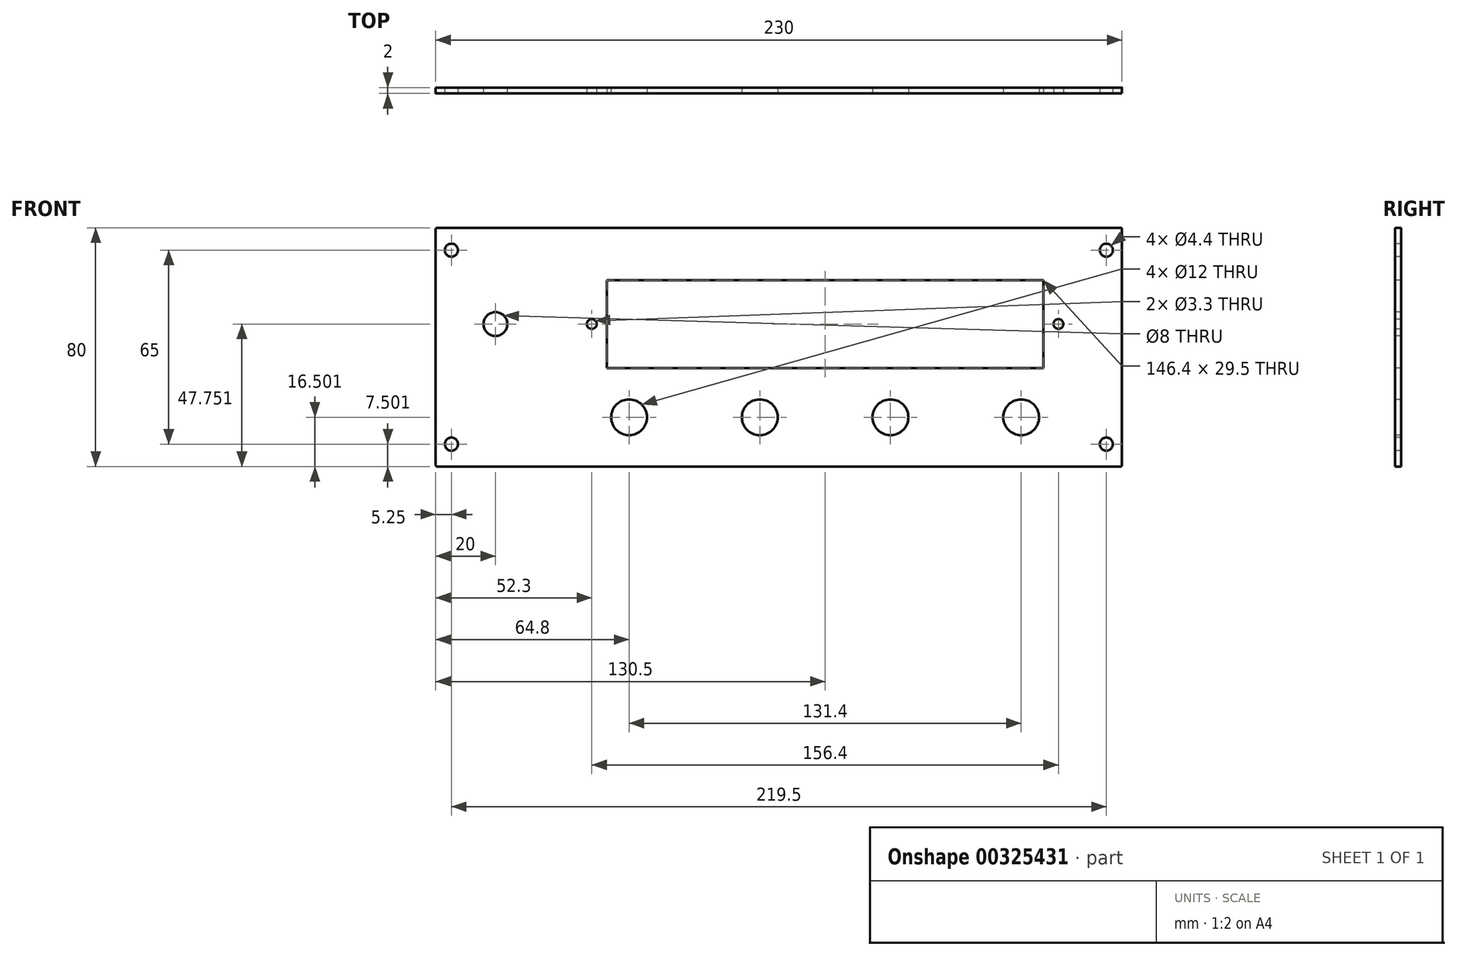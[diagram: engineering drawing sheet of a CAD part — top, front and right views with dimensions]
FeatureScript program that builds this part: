
annotation { "Feature Type Name" : "Feature", "Feature Type Description" : "" }
export const myFeature = defineFeature(function(context is Context, id is Id, definition is map)
    precondition{}
    {
        {
            var Q0;
            Q0=qCreatedBy(makeId("Front.planeOp"),FACE);
            var sketch = newSketch(context, id + "F0", { "sketchPlane" : qUnion([Q0])});
            skLineSegment(sketch, "E0.bottom", {"start": v(-114.5, 12.9) * mm, "end": v(114.5, 12.9) * mm});
            skLineSegment(sketch, "E0.top", {"start": v(-114.5, -67.1) * mm, "end": v(114.5, -67.1) * mm});
            skLineSegment(sketch, "E0.left", {"start": v(-115, 12.4) * mm, "end": v(-115, -66.6) * mm});
            skLineSegment(sketch, "E0.right", {"start": v(115, 12.4) * mm, "end": v(115, -66.6) * mm});
            skLineSegment(sketch, "E1", {"start": v(-115, 5.4) * mm, "end": v(115, 5.4) * mm, "construction": true});
            skLineSegment(sketch, "E2", {"start": v(-109.75, 12.9) * mm, "end": v(-109.75, -67.1) * mm, "construction": true});
            skPoint(sketch, "E3", {"position": v(-109.75, 5.4) * mm});
            skLineSegment(sketch, "E4.bottom", {"start": v(-57.7, -4.6) * mm, "end": v(88.7, -4.6) * mm});
            skLineSegment(sketch, "E4.top", {"start": v(-57.7, -34.1) * mm, "end": v(88.7, -34.1) * mm});
            skLineSegment(sketch, "E4.left", {"start": v(-57.7, -4.6) * mm, "end": v(-57.7, -34.1) * mm});
            skLineSegment(sketch, "E4.right", {"start": v(88.7, -4.6) * mm, "end": v(88.7, -34.1) * mm});
            skLineSegment(sketch, "E5", {"start": v(-62.7, -4.6) * mm, "end": v(-62.7, -34.1) * mm, "construction": true});
            skLineSegment(sketch, "E6", {"start": v(15.5, -4.6) * mm, "end": v(15.5, -34.1) * mm, "construction": true});
            skPoint(sketch, "E7", {"position": v(-62.7, -19.36) * mm});
            skPoint(sketch, "E8.MirrorP", {"position": v(93.7, -19.36) * mm});
            skLineSegment(sketch, "E9", {"start": v(0, 12.9) * mm, "end": v(0, -67.1) * mm, "construction": true});
            skLineSegment(sketch, "E10", {"start": v(-105, 12.9) * mm, "end": v(-105, -67.1) * mm, "construction": true});
            skLineSegment(sketch, "E11.MirrorCS", {"start": v(105, 12.9) * mm, "end": v(105, -67.1) * mm, "construction": true});
            skLineSegment(sketch, "E12.bottom", {"start": v(-66, -3.6) * mm, "end": v(97, -3.6) * mm, "construction": true});
            skLineSegment(sketch, "E12.top", {"start": v(-66, -35.1) * mm, "end": v(97, -35.1) * mm, "construction": true});
            skLineSegment(sketch, "E12.left", {"start": v(-66, -3.6) * mm, "end": v(-66, -35.1) * mm, "construction": true});
            skLineSegment(sketch, "E12.right", {"start": v(97, -3.6) * mm, "end": v(97, -35.1) * mm, "construction": true});
            skPoint(sketch, "E13", {"position": v(15.5, -3.6) * mm});
            skPoint(sketch, "E14", {"position": v(97, -19.36) * mm});
            skLineSegment(sketch, "E15", {"start": v(-62.7, -19.36) * mm, "end": v(93.7, -19.36) * mm, "construction": true});
            skPoint(sketch, "E16", {"position": v(-109.75, -59.6) * mm});
            skPoint(sketch, "E17.MirrorP", {"position": v(109.75, 5.4) * mm});
            skPoint(sketch, "E18.MirrorP", {"position": v(109.75, -59.6) * mm});
            skLineSegment(sketch, "E19", {"start": v(-105, -50.6) * mm, "end": v(105, -50.6) * mm, "construction": true});
            skPoint(sketch, "E20", {"position": v(-95, -19.36) * mm});
            skCircle(sketch, "E21", {"center": v(-95, -19.36) * mm, "radius": 6 * mm, "construction": true});
            skCircle(sketch, "E22", {"center": v(81.2, -50.6) * mm, "radius": 7.5 * mm, "construction": true});
            skCircle(sketch, "E23.1.0.0", {"center": v(37.4, -50.6) * mm, "radius": 7.5 * mm, "construction": true});
            skCircle(sketch, "E23.2.0.0", {"center": v(-6.4, -50.6) * mm, "radius": 7.5 * mm, "construction": true});
            skCircle(sketch, "E23.3.0.0", {"center": v(-50.2, -50.6) * mm, "radius": 7.5 * mm, "construction": true});
            skLineSegment(sketch, "E23.direction1", {"start": v(81.2, -50.6) * mm, "end": v(37.4, -50.6) * mm, "construction": true});
            skPoint(sketch, "E24.visualSharp", {"position": v(-115, 12.9) * mm});
            skArc(sketch, "E24.filletArc", {"start": v(-114.5, 12.9) * mm, "mid": v(-114.85, 12.74) * mm, "end": v(-115, 12.4) * mm});
            skPoint(sketch, "E25.visualSharp", {"position": v(-115, -67.1) * mm});
            skArc(sketch, "E25.filletArc", {"start": v(-115, -66.6) * mm, "mid": v(-114.85, -66.96) * mm, "end": v(-114.5, -67.1) * mm});
            skPoint(sketch, "E26.visualSharp", {"position": v(115, -67.1) * mm});
            skArc(sketch, "E26.filletArc", {"start": v(114.5, -67.1) * mm, "mid": v(114.85, -66.96) * mm, "end": v(115, -66.6) * mm});
            skPoint(sketch, "E27.visualSharp", {"position": v(115, 12.9) * mm});
            skArc(sketch, "E27.filletArc", {"start": v(115, 12.4) * mm, "mid": v(114.85, 12.74) * mm, "end": v(114.5, 12.9) * mm});
            skSolve(sketch);
        }
        {
            var Q0;
            Q0=makeQuery(id+"F0.imprint","IMPRINT",FACE,{"disambiguationData":[TD([[makeQuery(id+"F0.imprint","IMPRINT",EDGE,{"derivedFrom":sQuery(id+"F0.wireOp",EDGE,"E0.bottom")}),-1.0]])]});
            extrude(context, id + "F1", {"entities" : qUnion([Q0]), "oppositeDirection" : true, "depth" : 2 * mm});
        }
        {
            var Q0;
            Q0=sQuery(id+"F0.wireOp",VERTEX,"E3");
            var Q1;
            Q1=sQuery(id+"F0.wireOp",VERTEX,"E17.MirrorP");
            var Q2;
            Q2=sQuery(id+"F0.wireOp",VERTEX,"E18.MirrorP");
            var Q3;
            Q3=sQuery(id+"F0.wireOp",VERTEX,"E16");
            var Q4;
            Q4=makeQuery(id+"F1.opExtrude","SWEPT_BODY",BODY,{"disambiguationData":[OSD([sQuery(id+"F0.wireOp",EDGE,"E0.bottom"),sQuery(id+"F0.wireOp",EDGE,"E0.top"),sQuery(id+"F0.wireOp",EDGE,"E0.left"),sQuery(id+"F0.wireOp",EDGE,"E0.right"),sQuery(id+"F0.wireOp",EDGE,"wUSLe2jA-Vntq-9wAi-NqRe-D4dN2Iv6WiXZ"),sQuery(id+"F0.wireOp",EDGE,"0V3KryEC-EEOE-b1Vl-SPv9-SGiPuqfbHOCA"),sQuery(id+"F0.wireOp",EDGE,"VXoqg1l5-3Q0s-zM9H-MVhQ-kMZ0NWrAAzfJ")])]});
            hole(context, id + "F2", {"style" : HoleStyle.SIMPLE, "endStyle" : HoleEndStyle.THROUGH, "standardTappedOrClearance" : lookupTablePath({ "standard" : "ISO", "fit" : "Normal", "size" : "M4", "type" : "Clearance" }), "standardBlindInLast" : lookupTablePath({ "fit" : "Standard", "standard" : "ISO", "size" : "M4", "type" : "Clearance" }), "holeDiameter" : 4.4 * mm, "tappedDepth" : 12 * mm, "tapClearance" : 3, "locations" : qUnion([Q0, Q1, Q2, Q3]), "scope" : qUnion([Q4])});
        }
        {
            var Q0;
            Q0=sQuery(id+"F0.wireOp",VERTEX,"E7");
            var Q1;
            Q1=sQuery(id+"F0.wireOp",VERTEX,"E8.MirrorP");
            var Q2;
            Q2=makeQuery(id+"F1.opExtrude","SWEPT_BODY",BODY,{"disambiguationData":[OSD([sQuery(id+"F0.wireOp",EDGE,"E0.bottom"),sQuery(id+"F0.wireOp",EDGE,"E0.top"),sQuery(id+"F0.wireOp",EDGE,"E0.left"),sQuery(id+"F0.wireOp",EDGE,"E0.right"),sQuery(id+"F0.wireOp",EDGE,"E4.bottom"),sQuery(id+"F0.wireOp",EDGE,"E4.top"),sQuery(id+"F0.wireOp",EDGE,"E4.left"),sQuery(id+"F0.wireOp",EDGE,"E4.right")])]});
            hole(context, id + "F3", {"style" : HoleStyle.SIMPLE, "endStyle" : HoleEndStyle.THROUGH, "standardTappedOrClearance" : lookupTablePath({ "standard" : "ISO", "fit" : "Normal", "size" : "M3", "type" : "Clearance" }), "standardBlindInLast" : lookupTablePath({ "fit" : "Standard", "standard" : "ISO", "size" : "M3", "type" : "Clearance" }), "holeDiameter" : 3.3 * mm, "tappedDepth" : 12 * mm, "tapClearance" : 3, "locations" : qUnion([Q0, Q1]), "scope" : qUnion([Q2])});
        }
        {
            var Q0;
            Q0=sQuery(id+"F0.wireOp",VERTEX,"E20");
            var Q1;
            Q1=makeQuery(id+"F1.opExtrude","SWEPT_BODY",BODY,{"disambiguationData":[OSD([sQuery(id+"F0.wireOp",EDGE,"E0.bottom"),sQuery(id+"F0.wireOp",EDGE,"E0.top"),sQuery(id+"F0.wireOp",EDGE,"E0.left"),sQuery(id+"F0.wireOp",EDGE,"E0.right"),sQuery(id+"F0.wireOp",EDGE,"E4.bottom"),sQuery(id+"F0.wireOp",EDGE,"E4.top"),sQuery(id+"F0.wireOp",EDGE,"E4.left"),sQuery(id+"F0.wireOp",EDGE,"E4.right")])]});
            hole(context, id + "F4", {"style" : HoleStyle.SIMPLE, "endStyle" : HoleEndStyle.THROUGH, "holeDiameter" : 8 * mm, "tappedDepth" : 12 * mm, "tapClearance" : 3, "locations" : qUnion([Q0]), "scope" : qUnion([Q1])});
        }
        {
            var Q0;
            Q0=sQuery(id+"F0.wireOp",VERTEX,"E23.3.0.0.center");
            var Q1;
            Q1=sQuery(id+"F0.wireOp",VERTEX,"E23.2.0.0.center");
            var Q2;
            Q2=sQuery(id+"F0.wireOp",VERTEX,"E23.direction1.end");
            var Q3;
            Q3=sQuery(id+"F0.wireOp",VERTEX,"E22.center");
            var Q4;
            Q4=makeQuery(id+"F1.opExtrude","SWEPT_BODY",BODY,{"disambiguationData":[OSD([sQuery(id+"F0.wireOp",EDGE,"E0.bottom"),sQuery(id+"F0.wireOp",EDGE,"E0.top"),sQuery(id+"F0.wireOp",EDGE,"E0.left"),sQuery(id+"F0.wireOp",EDGE,"E0.right"),sQuery(id+"F0.wireOp",EDGE,"E4.bottom"),sQuery(id+"F0.wireOp",EDGE,"E4.top"),sQuery(id+"F0.wireOp",EDGE,"E4.left"),sQuery(id+"F0.wireOp",EDGE,"E4.right"),sQuery(id+"F0.wireOp",EDGE,"be85724a-6f3b-4295-9a29-0f0e669f6d4a.sketch_text.stroke-0"),sQuery(id+"F0.wireOp",EDGE,"be85724a-6f3b-4295-9a29-0f0e669f6d4a.sketch_text.stroke-1"),sQuery(id+"F0.wireOp",EDGE,"be85724a-6f3b-4295-9a29-0f0e669f6d4a.sketch_text.stroke-2"),sQuery(id+"F0.wireOp",EDGE,"be85724a-6f3b-4295-9a29-0f0e669f6d4a.sketch_text.stroke-3"),sQuery(id+"F0.wireOp",EDGE,"be85724a-6f3b-4295-9a29-0f0e669f6d4a.sketch_text.stroke-4"),sQuery(id+"F0.wireOp",EDGE,"be85724a-6f3b-4295-9a29-0f0e669f6d4a.sketch_text.stroke-5"),sQuery(id+"F0.wireOp",EDGE,"be85724a-6f3b-4295-9a29-0f0e669f6d4a.sketch_text.stroke-6"),sQuery(id+"F0.wireOp",EDGE,"be85724a-6f3b-4295-9a29-0f0e669f6d4a.sketch_text.stroke-7"),sQuery(id+"F0.wireOp",EDGE,"be85724a-6f3b-4295-9a29-0f0e669f6d4a.sketch_text.stroke-8"),sQuery(id+"F0.wireOp",EDGE,"be85724a-6f3b-4295-9a29-0f0e669f6d4a.sketch_text.stroke-9"),sQuery(id+"F0.wireOp",EDGE,"be85724a-6f3b-4295-9a29-0f0e669f6d4a.sketch_text.stroke-10"),sQuery(id+"F0.wireOp",EDGE,"be85724a-6f3b-4295-9a29-0f0e669f6d4a.sketch_text.stroke-11"),sQuery(id+"F0.wireOp",EDGE,"be85724a-6f3b-4295-9a29-0f0e669f6d4a.sketch_text.stroke-12"),sQuery(id+"F0.wireOp",EDGE,"be85724a-6f3b-4295-9a29-0f0e669f6d4a.sketch_text.stroke-13"),sQuery(id+"F0.wireOp",EDGE,"be85724a-6f3b-4295-9a29-0f0e669f6d4a.sketch_text.stroke-14"),sQuery(id+"F0.wireOp",EDGE,"be85724a-6f3b-4295-9a29-0f0e669f6d4a.sketch_text.stroke-15"),sQuery(id+"F0.wireOp",EDGE,"be85724a-6f3b-4295-9a29-0f0e669f6d4a.sketch_text.stroke-16"),sQuery(id+"F0.wireOp",EDGE,"be85724a-6f3b-4295-9a29-0f0e669f6d4a.sketch_text.stroke-17"),sQuery(id+"F0.wireOp",EDGE,"be85724a-6f3b-4295-9a29-0f0e669f6d4a.sketch_text.stroke-18"),sQuery(id+"F0.wireOp",EDGE,"be85724a-6f3b-4295-9a29-0f0e669f6d4a.sketch_text.stroke-19"),sQuery(id+"F0.wireOp",EDGE,"be85724a-6f3b-4295-9a29-0f0e669f6d4a.sketch_text.stroke-20"),sQuery(id+"F0.wireOp",EDGE,"be85724a-6f3b-4295-9a29-0f0e669f6d4a.sketch_text.stroke-21"),sQuery(id+"F0.wireOp",EDGE,"be85724a-6f3b-4295-9a29-0f0e669f6d4a.sketch_text.stroke-22"),sQuery(id+"F0.wireOp",EDGE,"be85724a-6f3b-4295-9a29-0f0e669f6d4a.sketch_text.stroke-23"),sQuery(id+"F0.wireOp",EDGE,"be85724a-6f3b-4295-9a29-0f0e669f6d4a.sketch_text.stroke-24"),sQuery(id+"F0.wireOp",EDGE,"be85724a-6f3b-4295-9a29-0f0e669f6d4a.sketch_text.stroke-25"),sQuery(id+"F0.wireOp",EDGE,"be85724a-6f3b-4295-9a29-0f0e669f6d4a.sketch_text.stroke-26"),sQuery(id+"F0.wireOp",EDGE,"be85724a-6f3b-4295-9a29-0f0e669f6d4a.sketch_text.stroke-27"),sQuery(id+"F0.wireOp",EDGE,"be85724a-6f3b-4295-9a29-0f0e669f6d4a.sketch_text.stroke-28"),sQuery(id+"F0.wireOp",EDGE,"be85724a-6f3b-4295-9a29-0f0e669f6d4a.sketch_text.stroke-29"),sQuery(id+"F0.wireOp",EDGE,"be85724a-6f3b-4295-9a29-0f0e669f6d4a.sketch_text.stroke-30"),sQuery(id+"F0.wireOp",EDGE,"be85724a-6f3b-4295-9a29-0f0e669f6d4a.sketch_text.stroke-31"),sQuery(id+"F0.wireOp",EDGE,"be85724a-6f3b-4295-9a29-0f0e669f6d4a.sketch_text.stroke-32"),sQuery(id+"F0.wireOp",EDGE,"be85724a-6f3b-4295-9a29-0f0e669f6d4a.sketch_text.stroke-33"),sQuery(id+"F0.wireOp",EDGE,"be85724a-6f3b-4295-9a29-0f0e669f6d4a.sketch_text.stroke-34"),sQuery(id+"F0.wireOp",EDGE,"be85724a-6f3b-4295-9a29-0f0e669f6d4a.sketch_text.stroke-35"),sQuery(id+"F0.wireOp",EDGE,"be85724a-6f3b-4295-9a29-0f0e669f6d4a.sketch_text.stroke-36"),sQuery(id+"F0.wireOp",EDGE,"be85724a-6f3b-4295-9a29-0f0e669f6d4a.sketch_text.stroke-37"),sQuery(id+"F0.wireOp",EDGE,"be85724a-6f3b-4295-9a29-0f0e669f6d4a.sketch_text.stroke-38"),sQuery(id+"F0.wireOp",EDGE,"be85724a-6f3b-4295-9a29-0f0e669f6d4a.sketch_text.stroke-39"),sQuery(id+"F0.wireOp",EDGE,"be85724a-6f3b-4295-9a29-0f0e669f6d4a.sketch_text.stroke-40"),sQuery(id+"F0.wireOp",EDGE,"be85724a-6f3b-4295-9a29-0f0e669f6d4a.sketch_text.stroke-41"),sQuery(id+"F0.wireOp",EDGE,"be85724a-6f3b-4295-9a29-0f0e669f6d4a.sketch_text.stroke-42"),sQuery(id+"F0.wireOp",EDGE,"be85724a-6f3b-4295-9a29-0f0e669f6d4a.sketch_text.stroke-43"),sQuery(id+"F0.wireOp",EDGE,"be85724a-6f3b-4295-9a29-0f0e669f6d4a.sketch_text.stroke-44"),sQuery(id+"F0.wireOp",EDGE,"be85724a-6f3b-4295-9a29-0f0e669f6d4a.sketch_text.stroke-45"),sQuery(id+"F0.wireOp",EDGE,"be85724a-6f3b-4295-9a29-0f0e669f6d4a.sketch_text.stroke-46"),sQuery(id+"F0.wireOp",EDGE,"be85724a-6f3b-4295-9a29-0f0e669f6d4a.sketch_text.stroke-47"),sQuery(id+"F0.wireOp",EDGE,"be85724a-6f3b-4295-9a29-0f0e669f6d4a.sketch_text.stroke-48"),sQuery(id+"F0.wireOp",EDGE,"be85724a-6f3b-4295-9a29-0f0e669f6d4a.sketch_text.stroke-49"),sQuery(id+"F0.wireOp",EDGE,"be85724a-6f3b-4295-9a29-0f0e669f6d4a.sketch_text.stroke-50"),sQuery(id+"F0.wireOp",EDGE,"be85724a-6f3b-4295-9a29-0f0e669f6d4a.sketch_text.stroke-51"),sQuery(id+"F0.wireOp",EDGE,"be85724a-6f3b-4295-9a29-0f0e669f6d4a.sketch_text.stroke-52"),sQuery(id+"F0.wireOp",EDGE,"be85724a-6f3b-4295-9a29-0f0e669f6d4a.sketch_text.stroke-53"),sQuery(id+"F0.wireOp",EDGE,"be85724a-6f3b-4295-9a29-0f0e669f6d4a.sketch_text.stroke-54"),sQuery(id+"F0.wireOp",EDGE,"be85724a-6f3b-4295-9a29-0f0e669f6d4a.sketch_text.stroke-55"),sQuery(id+"F0.wireOp",EDGE,"be85724a-6f3b-4295-9a29-0f0e669f6d4a.sketch_text.stroke-56"),sQuery(id+"F0.wireOp",EDGE,"be85724a-6f3b-4295-9a29-0f0e669f6d4a.sketch_text.stroke-57"),sQuery(id+"F0.wireOp",EDGE,"be85724a-6f3b-4295-9a29-0f0e669f6d4a.sketch_text.stroke-58"),sQuery(id+"F0.wireOp",EDGE,"be85724a-6f3b-4295-9a29-0f0e669f6d4a.sketch_text.stroke-59"),sQuery(id+"F0.wireOp",EDGE,"be85724a-6f3b-4295-9a29-0f0e669f6d4a.sketch_text.stroke-60"),sQuery(id+"F0.wireOp",EDGE,"be85724a-6f3b-4295-9a29-0f0e669f6d4a.sketch_text.stroke-61"),sQuery(id+"F0.wireOp",EDGE,"be85724a-6f3b-4295-9a29-0f0e669f6d4a.sketch_text.stroke-62"),sQuery(id+"F0.wireOp",EDGE,"be85724a-6f3b-4295-9a29-0f0e669f6d4a.sketch_text.stroke-63"),sQuery(id+"F0.wireOp",EDGE,"be85724a-6f3b-4295-9a29-0f0e669f6d4a.sketch_text.stroke-70"),sQuery(id+"F0.wireOp",EDGE,"be85724a-6f3b-4295-9a29-0f0e669f6d4a.sketch_text.stroke-71"),sQuery(id+"F0.wireOp",EDGE,"be85724a-6f3b-4295-9a29-0f0e669f6d4a.sketch_text.stroke-72"),sQuery(id+"F0.wireOp",EDGE,"be85724a-6f3b-4295-9a29-0f0e669f6d4a.sketch_text.stroke-73"),sQuery(id+"F0.wireOp",EDGE,"be85724a-6f3b-4295-9a29-0f0e669f6d4a.sketch_text.stroke-74"),sQuery(id+"F0.wireOp",EDGE,"be85724a-6f3b-4295-9a29-0f0e669f6d4a.sketch_text.stroke-75"),sQuery(id+"F0.wireOp",EDGE,"be85724a-6f3b-4295-9a29-0f0e669f6d4a.sketch_text.stroke-76"),sQuery(id+"F0.wireOp",EDGE,"be85724a-6f3b-4295-9a29-0f0e669f6d4a.sketch_text.stroke-77")])]});
            hole(context, id + "F5", {"style" : HoleStyle.SIMPLE, "endStyle" : HoleEndStyle.THROUGH, "holeDiameter" : 12 * mm, "tappedDepth" : 12 * mm, "tapClearance" : 3, "locations" : qUnion([Q0, Q1, Q2, Q3]), "scope" : qUnion([Q4])});
        }
    });
